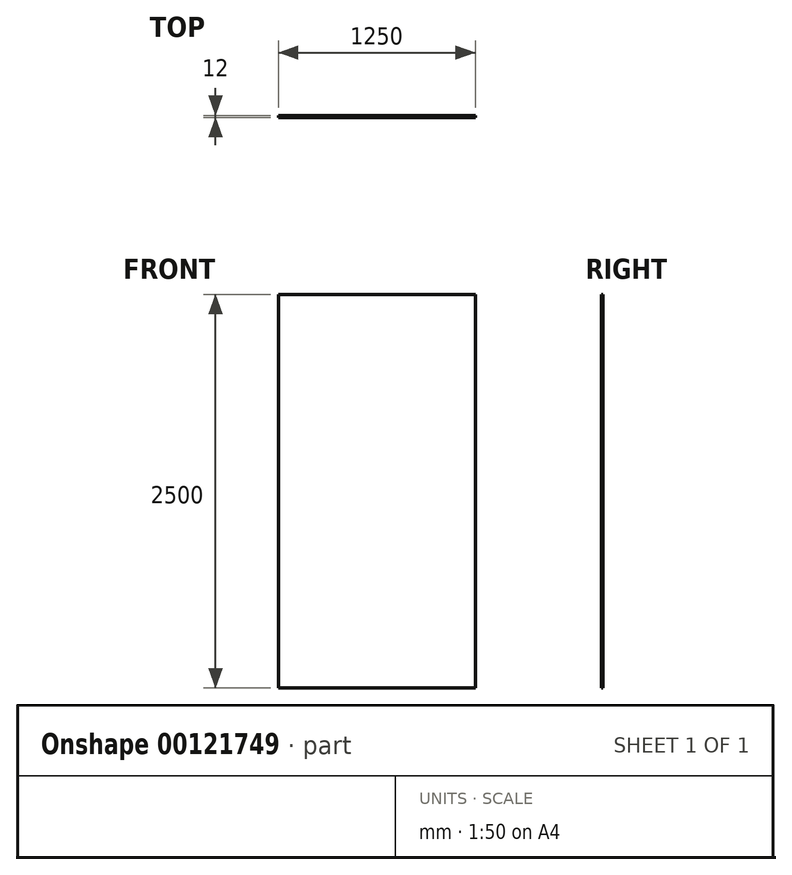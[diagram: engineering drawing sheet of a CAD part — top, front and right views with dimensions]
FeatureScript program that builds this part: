
annotation { "Feature Type Name" : "Feature", "Feature Type Description" : "" }
export const myFeature = defineFeature(function(context is Context, id is Id, definition is map)
    precondition{}
    {
        {
            assignVariable(context, id + "F0", {"name" : "zosb", "anyValue" : 12});
        }
        {
            assignVariable(context, id + "F6", {"name" : "zpps", "anyValue" : 200});
        }
        {
            var Q0;
            Q0=qCreatedBy(makeId("Front.planeOp"),FACE);
            var sketch = newSketch(context, id + "F7", { "sketchPlane" : qUnion([Q0])});
            skLineSegment(sketch, "E0.bottom", {"start": v(625, -1250) * mm, "end": v(-625, -1250) * mm});
            skLineSegment(sketch, "E0.top", {"start": v(625, 1250) * mm, "end": v(-625, 1250) * mm});
            skLineSegment(sketch, "E0.left", {"start": v(625, -1250) * mm, "end": v(625, 1250) * mm});
            skLineSegment(sketch, "E0.right", {"start": v(-625, -1250) * mm, "end": v(-625, 1250) * mm});
            skPoint(sketch, "E0.middle", {"position": v(0, 0) * mm});
            skSolve(sketch);
        }
        {
            var Q0;
            Q0 = qSketchRegion(id + "F7", true);
            extrude(context, id + "F1", {"entities" : qUnion([Q0]), "oppositeDirection" : true, "depth" : (getVariable(context, 'zosb')) * mm});
        }
        {
            var Q0;
            Q0=makeQuery(id+"F1.opExtrude","CAP_FACE",FACE,{"disambiguationData":[OSD([sQuery(id+"F7.wireOp",EDGE,"E0.bottom"),sQuery(id+"F7.wireOp",EDGE,"E0.top"),sQuery(id+"F7.wireOp",EDGE,"E0.left"),sQuery(id+"F7.wireOp",EDGE,"E0.right")])],"isStart":true});
            var sketch = newSketch(context, id + "F8", { "sketchPlane" : qUnion([Q0])});
            skLineSegment(sketch, "E1.bottom", {"start": v(575, -1200) * mm, "end": v(-575, -1200) * mm});
            skLineSegment(sketch, "E1.top", {"start": v(575, 1200) * mm, "end": v(-575, 1200) * mm});
            skLineSegment(sketch, "E1.left", {"start": v(575, -1200) * mm, "end": v(575, 1200) * mm});
            skLineSegment(sketch, "E1.right", {"start": v(-575, -1200) * mm, "end": v(-575, 1200) * mm});
            skPoint(sketch, "E1.middle", {"position": v(0, 0) * mm});
            skSolve(sketch);
        }
        {
            var Q0;
            Q0 = qSketchRegion(id + "F8", true);
            extrude(context, id + "F2", {"entities" : qUnion([Q0]), "depth" : (getVariable(context, 'zpps')) * mm});
        }
        {
            var Q0;
            Q0=makeQuery(id+"F2.opExtrude","CAP_FACE",FACE,{"disambiguationData":[OSD([sQuery(id+"F8.wireOp",EDGE,"E1.bottom"),sQuery(id+"F8.wireOp",EDGE,"E1.top"),sQuery(id+"F8.wireOp",EDGE,"E1.left"),sQuery(id+"F8.wireOp",EDGE,"E1.right")])],"isStart":false});
            var sketch = newSketch(context, id + "F3", { "sketchPlane" : qUnion([Q0])});
            skLineSegment(sketch, "E2.bottom", {"start": v(625, -1250) * mm, "end": v(-625, -1250) * mm});
            skLineSegment(sketch, "E2.top", {"start": v(625, 1250) * mm, "end": v(-625, 1250) * mm});
            skLineSegment(sketch, "E2.left", {"start": v(625, -1250) * mm, "end": v(625, 1250) * mm});
            skLineSegment(sketch, "E2.right", {"start": v(-625, -1250) * mm, "end": v(-625, 1250) * mm});
            skPoint(sketch, "E2.middle", {"position": v(0, 0) * mm});
            skSolve(sketch);
        }
        {
            var Q0;
            Q0 = qSketchRegion(id + "F3", true);
            extrude(context, id + "F4", {"entities" : qUnion([Q0]), "depth" : (getVariable(context, 'zosb')) * mm});
        }
        {
            var Q0;
            Q0=makeQuery(id+"F2.opExtrude","SWEPT_BODY",BODY,{"disambiguationData":[OSD([sQuery(id+"F8.wireOp",EDGE,"E1.bottom"),sQuery(id+"F8.wireOp",EDGE,"E1.top"),sQuery(id+"F8.wireOp",EDGE,"E1.left"),sQuery(id+"F8.wireOp",EDGE,"E1.right")])]});
            deleteBodies(context, id + "F9", {"entities" : qUnion([Q0])});
        }
        {
            var Q0;
            Q0=makeQuery(id+"F4.opExtrude","SWEPT_BODY",BODY,{"disambiguationData":[OSD([sQuery(id+"F3.wireOp",EDGE,"E2.bottom"),sQuery(id+"F3.wireOp",EDGE,"E2.top"),sQuery(id+"F3.wireOp",EDGE,"E2.left"),sQuery(id+"F3.wireOp",EDGE,"E2.right")])]});
            deleteBodies(context, id + "F5", {"entities" : qUnion([Q0])});
        }
    });
